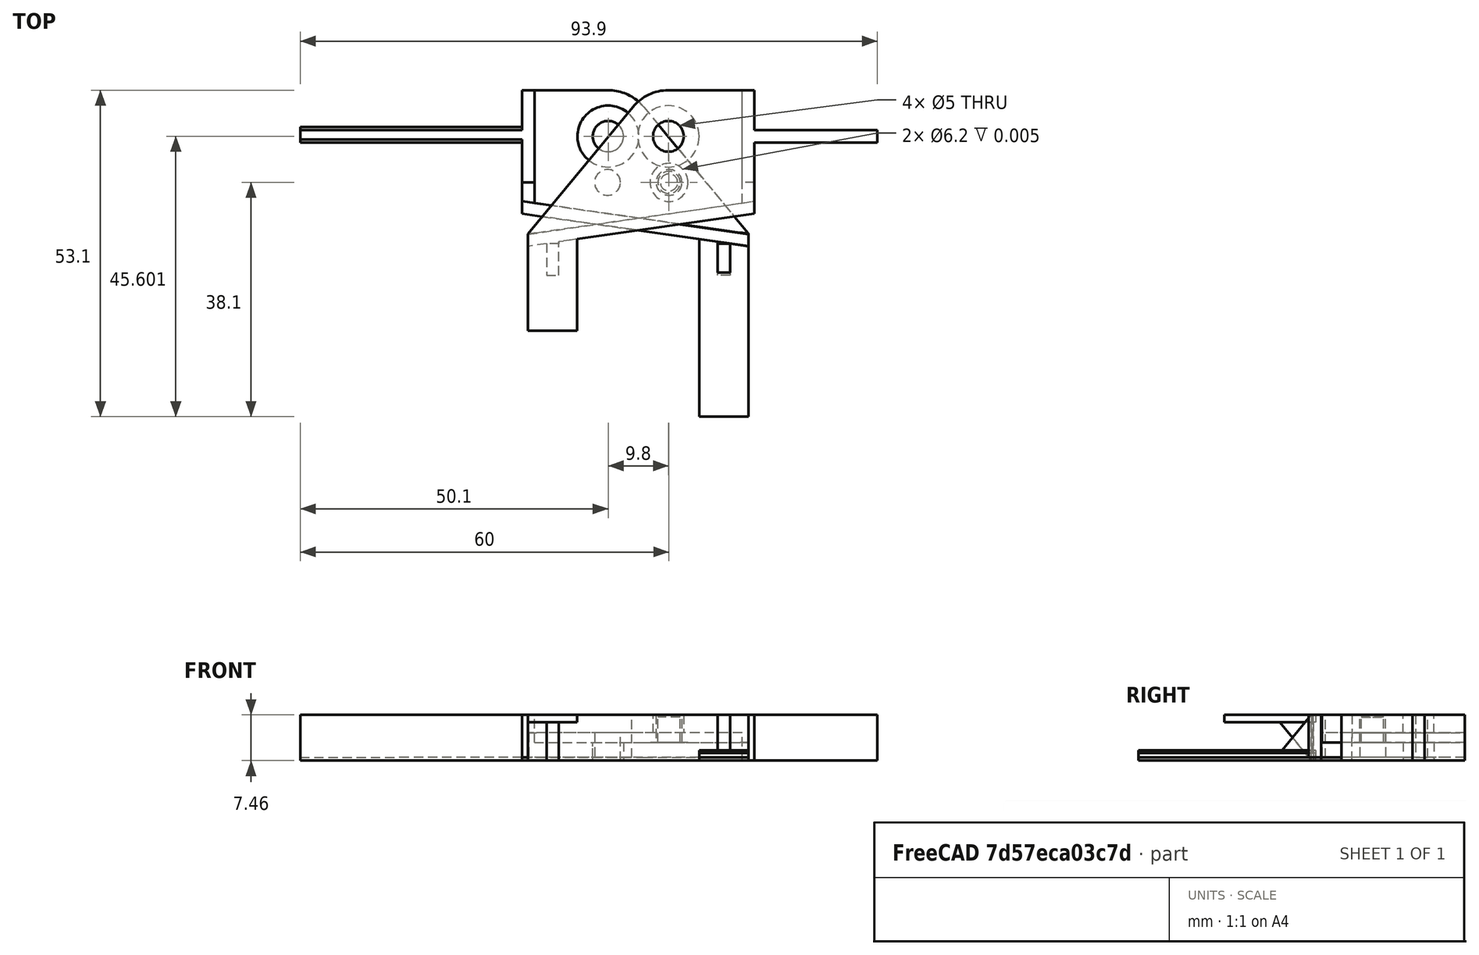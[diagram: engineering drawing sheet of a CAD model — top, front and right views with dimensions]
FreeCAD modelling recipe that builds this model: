
FCSTD DOCUMENT  (FreeCAD 0.18R16146 (Git))
Label: endstop-flag
License: All rights reserved
LicenseURL: http://en.wikipedia.org/wiki/All_rights_reserved
objects: Part::Feature×8, Part::Box×7, Part::MultiFuse×4, Part::Cut×4, Part::MultiCommon×3, Part::Cylinder×2, Part::Chamfer×1
note: 29 computed .brp shape members not serialized (recipe doc carries the construction recipe); baked Part::Feature solids carry a one-line shape summary decoded from their .brp

FEATURE [Part::Feature] Part__Feature067001001  label="flag-origin"
  shape: bbox 56.82 x 39.1 x 7.454 mm, 33 faces (baked)
FEATURE [Part::Feature] Part__Feature067001001001  label="flag-origin001"
  shape: bbox 56.82 x 39.1 x 7.454 mm, 33 faces (baked)
FEATURE [Part::Box] Box  label="Cube"
  AttacherType = Attacher::AttachEngine3D
  Height = 10
  Length = 10
  Placement = pos=(-19,-26,0) rot=(0,0,1;0rad)
  Width = 10
FEATURE [Part::Box] Box001  label="Cube001"
  AttacherType = Attacher::AttachEngine3D
  Height = 10
  Length = 17
  Placement = pos=(20,3,0) rot=(0,0,1;0rad)
  Width = 10
FEATURE [Part::Feature] Part__Feature067001001002  label="flag-origin002"
  shape: bbox 56.82 x 39.1 x 7.454 mm, 33 faces (baked)
FEATURE [Part::Feature] Part__Feature067001001003  label="flag-origin003"
  shape: bbox 56.82 x 39.1 x 7.454 mm, 33 faces (baked)
FEATURE [Part::MultiCommon] Common
  Placement = pos=(18,0,0) rot=(0,0,1;0rad)
  Shapes = -> [Part__Feature067001001002,Box001]
FEATURE [Part::MultiCommon] Common001
  Placement = pos=(0,-7,0) rot=(0,0,1;0rad)
  Shapes = -> [Box,Part__Feature067001001003]
FEATURE [Part::Feature] Common001001  label="Common002"
  Placement = pos=(0,-14,0) rot=(0,0,1;0rad)
  shape: bbox 8 x 8.044 x 1.2 mm, 6 faces (baked)
FEATURE [Part::MultiFuse] Fusion
  Placement = pos=(-2e-15,0,7.46) rot=(0,1,0;3.14159rad)
  Shapes = -> [Common001,Common001001,Part__Feature067001001001,Common]
FEATURE [Part::Box] Box002  label="Cube002"
  AttacherType = Attacher::AttachEngine3D
  Height = 10
  Length = 40
  Placement = pos=(-58.9,2,0) rot=(0,0,1;0rad)
  Width = 10
FEATURE [Part::Feature] Fusion001
  Placement = pos=(-2e-15,0,7.46) rot=(0,1,0;3.14159rad)
  shape: bbox 72.92 x 53.1 x 7.454 mm, 57 faces (baked)
FEATURE [Part::Feature] Fusion002
  Placement = pos=(-2e-15,0,7.46) rot=(0,1,0;3.14159rad)
  shape: bbox 72.92 x 53.1 x 7.454 mm, 57 faces (baked)
FEATURE [Part::Box] Box003  label="Cube003"
  AttacherType = Attacher::AttachEngine3D
  Height = 10
  Length = 40
  Placement = pos=(-58.9,2,0) rot=(0,0,1;0rad)
  Width = 10
FEATURE [Part::MultiCommon] Common001002
  Placement = pos=(0,0.5,0) rot=(0,0,1;0rad)
  Shapes = -> [Fusion001,Box002]
FEATURE [Part::Cut] Cut
  Base = -> Fusion002
  Tool = -> Box003
FEATURE [Part::MultiFuse] Fusion003
  Shapes = -> [Common001002,Cut]
FEATURE [Part::Box] Box004  label="Cube004"
  AttacherType = Attacher::AttachEngine3D
  Height = 0.5
  Length = 78
  Placement = pos=(-57,-40.5,0) rot=(0,0,1;0rad)
  Width = 66
FEATURE [Part::Cut] Cut001
  Base = -> Fusion003
  Tool = -> Box004
FEATURE [Part::Cylinder] Cylinder
  Angle = 360
  AttacherType = Attacher::AttachEngine3D
  Height = 10
  Placement = pos=(5,0.06,2.95) rot=(0,0,1;0rad)
  Radius = 3.1
FEATURE [Part::Cylinder] Cylinder001
  Angle = 360
  AttacherType = Attacher::AttachEngine3D
  Height = 4.5
  Placement = pos=(5,0.06,2.95) rot=(0,0,1;0rad)
  Radius = 1.8
FEATURE [Part::Cut] Cut002
  Base = -> Cut001
  Tool = -> Cylinder
FEATURE [Part::Box] Box005  label="Cube005"
  AttacherType = Attacher::AttachEngine3D
  Height = 1.2
  Length = 8
  Placement = pos=(9.92,-38.04,0.5) rot=(0,0,1;0rad)
  Width = 29
FEATURE [Part::MultiFuse] Fusion004
  Shapes = -> [Box005,Cut002]
FEATURE [Part::Chamfer] Chamfer
  Base = -> Cylinder001
  Edges = 1 edges r=0.4: [Edge1]
FEATURE [Part::MultiFuse] Fusion005  label="left"
  Shapes = -> [Chamfer,Fusion004]
FEATURE [Part::Feature] Fusion005001  label="left001"
  Placement = pos=(0,0,0) rot=(0,0,1;0.142768rad)
  shape: bbox 78.88 x 50.53 x 6.955 mm, 61 faces (baked)
FEATURE [Part::Box] Box006  label="Cube006"
  AttacherType = Attacher::AttachEngine3D
  Height = 10
  Length = 48
  Placement = pos=(0,-41.66,0) rot=(0,0,1;0rad)
  Width = 34
FEATURE [Part::Cut] Cut003  label="left-cut"
  Base = -> Fusion005001
  Placement = pos=(0,0,0) rot=(0,0,1;6.14042rad)
  Tool = -> Box006
